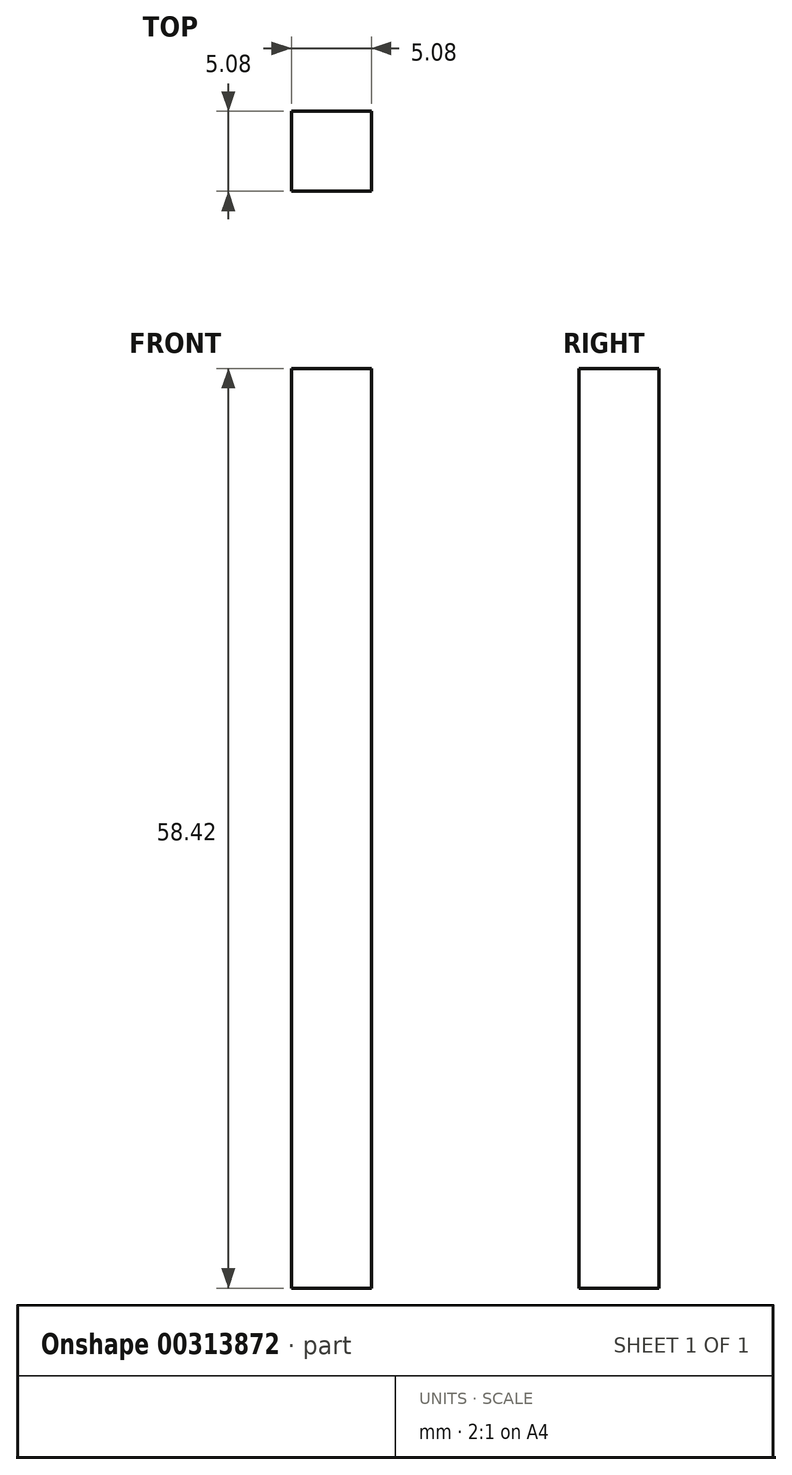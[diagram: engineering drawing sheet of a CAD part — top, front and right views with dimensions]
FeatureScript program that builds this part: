
annotation { "Feature Type Name" : "Feature", "Feature Type Description" : "" }
export const myFeature = defineFeature(function(context is Context, id is Id, definition is map)
    precondition{}
    {
        {
            var Q0;
            Q0=qCreatedBy(makeId("Front.planeOp"),FACE);
            var sketch = newSketch(context, id + "F0", { "sketchPlane" : qUnion([Q0])});
            skLineSegment(sketch, "E0.bottom", {"start": v(-56.5, 49.26) * mm, "end": v(-61.59, 49.26) * mm});
            skLineSegment(sketch, "E0.top", {"start": v(-56.5, -9.16) * mm, "end": v(-61.59, -9.16) * mm});
            skLineSegment(sketch, "E0.left", {"start": v(-56.5, 49.26) * mm, "end": v(-56.5, -9.16) * mm});
            skLineSegment(sketch, "E0.right", {"start": v(-61.59, 49.26) * mm, "end": v(-61.59, -9.16) * mm});
            skSolve(sketch);
        }
        {
            var Q0;
            Q0=makeQuery(id+"F0.imprint","IMPRINT",FACE,{"disambiguationData":[TD([[makeQuery(id+"F0.imprint","IMPRINT",EDGE,{"derivedFrom":sQuery(id+"F0.wireOp",EDGE,"E0.bottom")}),1.0]])]});
            extrude(context, id + "F1", {"entities" : qUnion([Q0]), "depth" : 5.08 * mm});
        }
    });
